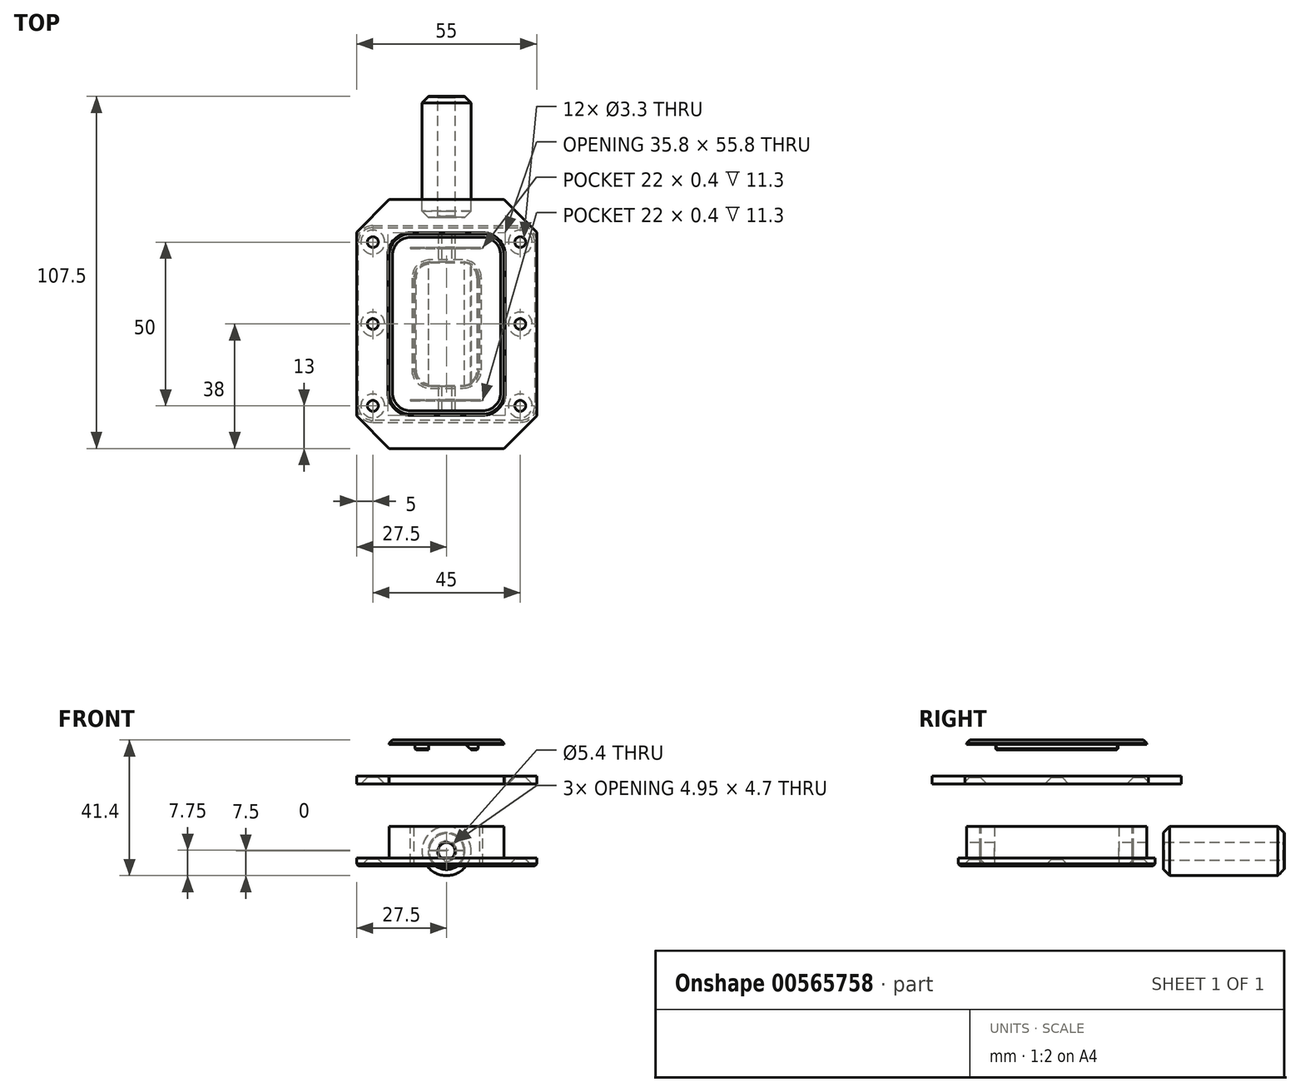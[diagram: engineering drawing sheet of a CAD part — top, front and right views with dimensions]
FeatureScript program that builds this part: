
annotation { "Feature Type Name" : "Feature", "Feature Type Description" : "" }
export const myFeature = defineFeature(function(context is Context, id is Id, definition is map)
    precondition{}
    {
        {
            var Q0;
            Q0=qCreatedBy(makeId("Top.planeOp"),FACE);
            cPlane(context, id + "F0", {"entities" : qUnion([Q0]), "cplaneType" : CPlaneType.OFFSET, "offset" : 25 * mm, "width" : 150 * mm, "height" : 150 * mm});
        }
        {
            var Q0;
            Q0=qCreatedBy(makeId("Top.planeOp"),FACE);
            var sketch = newSketch(context, id + "F1", { "sketchPlane" : qUnion([Q0])});
            skLineSegment(sketch, "E0.bottom", {"start": v(-22.5, 30) * mm, "end": v(22.5, 30) * mm});
            skLineSegment(sketch, "E0.top", {"start": v(-22.5, -30) * mm, "end": v(22.5, -30) * mm});
            skLineSegment(sketch, "E0.left", {"start": v(-27.5, 25) * mm, "end": v(-27.5, -25) * mm});
            skLineSegment(sketch, "E0.right", {"start": v(27.5, 25) * mm, "end": v(27.5, -25) * mm});
            skPoint(sketch, "E1.visualSharp", {"position": v(-27.5, 30) * mm});
            skArc(sketch, "E1.filletArc", {"start": v(-22.5, 30) * mm, "mid": v(-26.04, 28.54) * mm, "end": v(-27.5, 25) * mm});
            skPoint(sketch, "E2.visualSharp", {"position": v(27.5, 30) * mm});
            skArc(sketch, "E2.filletArc", {"start": v(27.5, 25) * mm, "mid": v(26.04, 28.54) * mm, "end": v(22.5, 30) * mm});
            skPoint(sketch, "E3.visualSharp", {"position": v(-27.5, -30) * mm});
            skArc(sketch, "E3.filletArc", {"start": v(-27.5, -25) * mm, "mid": v(-26.04, -28.54) * mm, "end": v(-22.5, -30) * mm});
            skPoint(sketch, "E4.visualSharp", {"position": v(27.5, -30) * mm});
            skArc(sketch, "E4.filletArc", {"start": v(22.5, -30) * mm, "mid": v(26.04, -28.54) * mm, "end": v(27.5, -25) * mm});
            skLineSegment(sketch, "E5.bottom", {"start": v(-5, 19) * mm, "end": v(5, 19) * mm});
            skLineSegment(sketch, "E5.top", {"start": v(-5, -19) * mm, "end": v(5, -19) * mm});
            skLineSegment(sketch, "E5.left", {"start": v(-10, 14) * mm, "end": v(-10, -14) * mm});
            skLineSegment(sketch, "E5.right", {"start": v(10, 14) * mm, "end": v(10, -14) * mm});
            skLineSegment(sketch, "E6", {"start": v(0, 19) * mm, "end": v(0, 30) * mm, "construction": true});
            skLineSegment(sketch, "E7", {"start": v(0, -19) * mm, "end": v(0, -30) * mm, "construction": true});
            skPoint(sketch, "E8.visualSharp", {"position": v(-10, 19) * mm});
            skArc(sketch, "E8.filletArc", {"start": v(-5, 19) * mm, "mid": v(-8.54, 17.54) * mm, "end": v(-10, 14) * mm});
            skPoint(sketch, "E9.visualSharp", {"position": v(10, 19) * mm});
            skArc(sketch, "E9.filletArc", {"start": v(10, 14) * mm, "mid": v(8.54, 17.54) * mm, "end": v(5, 19) * mm});
            skPoint(sketch, "E10.visualSharp", {"position": v(10, -19) * mm});
            skArc(sketch, "E10.filletArc", {"start": v(5, -19) * mm, "mid": v(8.54, -17.54) * mm, "end": v(10, -14) * mm});
            skPoint(sketch, "E11.visualSharp", {"position": v(-10, -19) * mm});
            skArc(sketch, "E11.filletArc", {"start": v(-10, -14) * mm, "mid": v(-8.54, -17.54) * mm, "end": v(-5, -19) * mm});
            skLineSegment(sketch, "E12", {"start": v(-27.5, 30) * mm, "end": v(27.5, -30) * mm, "construction": true});
            skLineSegment(sketch, "E13", {"start": v(27.5, 30) * mm, "end": v(-27.5, -30) * mm, "construction": true});
            skCircle(sketch, "E14", {"center": v(-22.5, 25) * mm, "radius": 1.65 * mm});
            skCircle(sketch, "E15", {"center": v(22.5, 25) * mm, "radius": 1.65 * mm});
            skCircle(sketch, "E16", {"center": v(22.5, -25) * mm, "radius": 1.65 * mm});
            skCircle(sketch, "E17", {"center": v(-22.5, -25) * mm, "radius": 1.65 * mm});
            skLineSegment(sketch, "E18", {"start": v(-22.5, 25) * mm, "end": v(-22.5, -25) * mm, "construction": true});
            skLineSegment(sketch, "E19", {"start": v(22.5, 25) * mm, "end": v(22.5, -25) * mm, "construction": true});
            skCircle(sketch, "E20", {"center": v(-22.5, 0) * mm, "radius": 1.65 * mm});
            skCircle(sketch, "E21", {"center": v(22.5, 0) * mm, "radius": 1.65 * mm});
            skSolve(sketch);
        }
        {
            var Q0;
            Q0=makeQuery(id+"F1.imprint","IMPRINT",FACE,{"disambiguationData":[TD([[makeQuery(id+"F1.imprint","IMPRINT",EDGE,{"derivedFrom":sQuery(id+"F1.wireOp",EDGE,"E0.bottom")}),-1.0]])]});
            extrude(context, id + "F2", {"entities" : qUnion([Q0]), "depth" : 2.4 * mm, "offsetDistance" : 25 * mm});
        }
        {
            var Q0;
            Q0=makeQuery(id+"F2.opExtrude","CAP_FACE",FACE,{"disambiguationData":[OSD([sQuery(id+"F1.wireOp",EDGE,"E0.bottom"),sQuery(id+"F1.wireOp",EDGE,"E0.top"),sQuery(id+"F1.wireOp",EDGE,"E0.left"),sQuery(id+"F1.wireOp",EDGE,"E0.right"),sQuery(id+"F1.wireOp",EDGE,"E1.filletArc"),sQuery(id+"F1.wireOp",EDGE,"E2.filletArc"),sQuery(id+"F1.wireOp",EDGE,"E3.filletArc"),sQuery(id+"F1.wireOp",EDGE,"E4.filletArc")])],"isStart":false});
            var sketch = newSketch(context, id + "F3", { "sketchPlane" : qUnion([Q0])});
            skArc(sketch, "E22.0.0", {"start": v(-27.5, -25) * mm, "mid": v(-26.04, -28.54) * mm, "end": v(-22.5, -30) * mm, "construction": true});
            skLineSegment(sketch, "E22.0.1", {"start": v(-22.5, -30) * mm, "end": v(22.5, -30) * mm, "construction": true});
            skArc(sketch, "E22.0.2", {"start": v(22.5, -30) * mm, "mid": v(26.04, -28.54) * mm, "end": v(27.5, -25) * mm, "construction": true});
            skLineSegment(sketch, "E22.0.3", {"start": v(27.5, -25) * mm, "end": v(27.5, 25) * mm, "construction": true});
            skArc(sketch, "E22.0.4", {"start": v(27.5, 25) * mm, "mid": v(26.04, 28.54) * mm, "end": v(22.5, 30) * mm, "construction": true});
            skLineSegment(sketch, "E22.0.5", {"start": v(22.5, 30) * mm, "end": v(-22.5, 30) * mm, "construction": true});
            skArc(sketch, "E22.0.6", {"start": v(-22.5, 30) * mm, "mid": v(-26.04, 28.54) * mm, "end": v(-27.5, 25) * mm, "construction": true});
            skLineSegment(sketch, "E22.0.7", {"start": v(-27.5, 25) * mm, "end": v(-27.5, -25) * mm, "construction": true});
            skLineSegment(sketch, "E23.bottom", {"start": v(-11, 27.5) * mm, "end": v(11, 27.5) * mm});
            skLineSegment(sketch, "E23.top", {"start": v(-11, -27.5) * mm, "end": v(11, -27.5) * mm});
            skLineSegment(sketch, "E23.left", {"start": v(-17.5, 21) * mm, "end": v(-17.5, -21) * mm});
            skLineSegment(sketch, "E23.right", {"start": v(17.5, 21) * mm, "end": v(17.5, -21) * mm});
            skLineSegment(sketch, "E24", {"start": v(0, 30) * mm, "end": v(0, 27.5) * mm, "construction": true});
            skLineSegment(sketch, "E25", {"start": v(0, -27.5) * mm, "end": v(0, -30) * mm, "construction": true});
            skPoint(sketch, "E26.visualSharp", {"position": v(-17.5, 27.5) * mm});
            skArc(sketch, "E26.filletArc", {"start": v(-11, 27.5) * mm, "mid": v(-15.6, 25.6) * mm, "end": v(-17.5, 21) * mm});
            skPoint(sketch, "E27.visualSharp", {"position": v(17.5, 27.5) * mm});
            skArc(sketch, "E27.filletArc", {"start": v(17.5, 21) * mm, "mid": v(15.6, 25.6) * mm, "end": v(11, 27.5) * mm});
            skPoint(sketch, "E28.visualSharp", {"position": v(-17.5, -27.5) * mm});
            skArc(sketch, "E28.filletArc", {"start": v(-17.5, -21) * mm, "mid": v(-15.6, -25.6) * mm, "end": v(-11, -27.5) * mm});
            skPoint(sketch, "E29.visualSharp", {"position": v(17.5, -27.5) * mm});
            skArc(sketch, "E29.filletArc", {"start": v(11, -27.5) * mm, "mid": v(15.6, -25.6) * mm, "end": v(17.5, -21) * mm});
            skSolve(sketch);
        }
        {
            var Q0;
            Q0=makeQuery(id+"F3.imprint","IMPRINT",FACE,{"disambiguationData":[TD([[makeQuery(id+"F3.imprint","IMPRINT",EDGE,{"derivedFrom":sQuery(id+"F3.wireOp",EDGE,"E23.bottom")}),-1.0]])]});
            extrude(context, id + "F4", {"entities" : qUnion([Q0]), "operationType" : NewBodyOperationType.ADD, "depth" : 9.6 * mm, "offsetDistance" : 25 * mm});
        }
        {
            var Q0;
            Q0=makeQuery(id+"F2.opExtrude","SWEPT_FACE",FACE,{"disambiguationData":[OSD([sQuery(id+"F1.wireOp",EDGE,"E0.top")])]});
            var sketch = newSketch(context, id + "F5", { "sketchPlane" : qUnion([Q0])});
            skLineSegment(sketch, "E30.0.0", {"start": v(-11, 2.4) * mm, "end": v(11, 2.4) * mm, "construction": true});
            skLineSegment(sketch, "E30.0.1", {"start": v(11, 2.4) * mm, "end": v(11, 12) * mm, "construction": true});
            skLineSegment(sketch, "E30.0.2", {"start": v(11, 12) * mm, "end": v(-11, 12) * mm});
            skLineSegment(sketch, "E30.0.3", {"start": v(-11, 12) * mm, "end": v(-11, 2.4) * mm, "construction": true});
            skLineSegment(sketch, "E31", {"start": v(-11, 4.5) * mm, "end": v(11, 4.5) * mm});
            skCircle(sketch, "E32", {"center": v(0, 4.5) * mm, "radius": 2.6 * mm});
            skCircle(sketch, "E33", {"center": v(0, 4.5) * mm, "radius": 7.5 * mm, "construction": true});
            skSolve(sketch);
        }
        {
            var Q0;
            {var subQ0=sQuery(id+"F5.wireOp",EDGE,"E32");var subQ1=sQuery(id+"F5.wireOp",EDGE,"E31");var subQ2=makeQuery(id+"F5.imprint","INTERSECT",VERTEX,{"disambiguationData":[OD(0.0)],"derivedFrom":[subQ1,subQ0]});Q0=makeQuery(id+"F5.imprint","IMPRINT",FACE,{"disambiguationData":[TD([[makeQuery(id+"F5.imprint","IMPRINT",EDGE,{"disambiguationData":[TD([[subQ2,-1.0]])],"derivedFrom":subQ1}),1.0]])]});}
            var Q1;
            {var subQ0=sQuery(id+"F5.wireOp",EDGE,"E32");var subQ1=sQuery(id+"F5.wireOp",EDGE,"E31");var subQ2=makeQuery(id+"F5.imprint","INTERSECT",VERTEX,{"disambiguationData":[OD(0.0)],"derivedFrom":[subQ1,subQ0]});Q1=makeQuery(id+"F5.imprint","IMPRINT",FACE,{"disambiguationData":[TD([[makeQuery(id+"F5.imprint","IMPRINT",EDGE,{"disambiguationData":[TD([[subQ2,-1.0]])],"derivedFrom":subQ1}),-1.0]])]});}
            var Q2;
            {var subQ0=sQuery(id+"F5.wireOp",EDGE,"E32");var subQ1=makeQuery(id+"F2.opExtrude","CAP_EDGE",EDGE,{"disambiguationData":[OSD([sQuery(id+"F1.wireOp",EDGE,"E0.top")])],"isStart":false});var subQ2=makeQuery(id+"F5.imprint","INTERSECT",VERTEX,{"disambiguationData":[OD(0.0)],"derivedFrom":[subQ1,subQ0]});Q2=makeQuery(id+"F5.imprint","IMPRINT",FACE,{"disambiguationData":[TD([[makeQuery(id+"F5.imprint","IMPRINT",EDGE,{"disambiguationData":[TD([[subQ2,-1.0]])],"derivedFrom":subQ0}),1.0]])]});}
            var Q3;
            Q3=makeQuery(id+"F2.opExtrude","SWEPT_FACE",FACE,{"disambiguationData":[OSD([sQuery(id+"F1.wireOp",EDGE,"E0.bottom")])]});
            extrude(context, id + "F6", {"entities" : qUnion([Q0, Q1, Q2]), "operationType" : NewBodyOperationType.REMOVE, "endBound" : BoundingType.UP_TO_SURFACE, "oppositeDirection" : true, "depth" : 25 * mm, "endBoundEntityFace" : qUnion([Q3]), "offsetDistance" : 25 * mm});
        }
        {
            var Q0;
            Q0=qCreatedBy(id+"F0.planeOp",FACE);
            var sketch = newSketch(context, id + "F7", { "sketchPlane" : qUnion([Q0])});
            skArc(sketch, "E34.0", {"start": v(22.5, -30) * mm, "mid": v(26.04, -28.54) * mm, "end": v(27.5, -25) * mm, "construction": true});
            skLineSegment(sketch, "E35.0", {"start": v(27.5, 25) * mm, "end": v(27.5, -25) * mm, "construction": true});
            skLineSegment(sketch, "E36.0", {"start": v(-22.5, -30) * mm, "end": v(22.5, -30) * mm, "construction": true});
            skLineSegment(sketch, "E37.0", {"start": v(-27.5, 25) * mm, "end": v(-27.5, -25) * mm, "construction": true});
            skArc(sketch, "E38.0", {"start": v(-27.5, -25) * mm, "mid": v(-26.04, -28.54) * mm, "end": v(-22.5, -30) * mm, "construction": true});
            skArc(sketch, "E38.1", {"start": v(-22.5, 30) * mm, "mid": v(-26.04, 28.54) * mm, "end": v(-27.5, 25) * mm, "construction": true});
            skLineSegment(sketch, "E38.2", {"start": v(-22.5, 30) * mm, "end": v(22.5, 30) * mm, "construction": true});
            skArc(sketch, "E39.0", {"start": v(27.5, 25) * mm, "mid": v(26.04, 28.54) * mm, "end": v(22.5, 30) * mm, "construction": true});
            skCircle(sketch, "E40.0", {"center": v(22.5, -25) * mm, "radius": 1.65 * mm});
            skCircle(sketch, "E41.0", {"center": v(22.5, 0) * mm, "radius": 1.65 * mm});
            skCircle(sketch, "E42.0", {"center": v(22.5, 25) * mm, "radius": 1.65 * mm});
            skCircle(sketch, "E43.0", {"center": v(-22.5, 25) * mm, "radius": 1.65 * mm});
            skCircle(sketch, "E44.0", {"center": v(-22.5, 0) * mm, "radius": 1.65 * mm});
            skCircle(sketch, "E45.0", {"center": v(-22.5, -25) * mm, "radius": 1.65 * mm});
            skArc(sketch, "E46.0", {"start": v(11, -27.5) * mm, "mid": v(15.6, -25.6) * mm, "end": v(17.5, -21) * mm, "construction": true});
            skLineSegment(sketch, "E47.0", {"start": v(17.5, 21) * mm, "end": v(17.5, -21) * mm, "construction": true});
            skArc(sketch, "E48.0", {"start": v(17.5, 21) * mm, "mid": v(15.6, 25.6) * mm, "end": v(11, 27.5) * mm, "construction": true});
            skLineSegment(sketch, "E49.0", {"start": v(-11, 27.5) * mm, "end": v(11, 27.5) * mm, "construction": true});
            skArc(sketch, "E50.0", {"start": v(-11, 27.5) * mm, "mid": v(-15.6, 25.6) * mm, "end": v(-17.5, 21) * mm, "construction": true});
            skLineSegment(sketch, "E51.0", {"start": v(-17.5, 21) * mm, "end": v(-17.5, -21) * mm, "construction": true});
            skArc(sketch, "E52.0", {"start": v(-17.5, -21) * mm, "mid": v(-15.6, -25.6) * mm, "end": v(-11, -27.5) * mm, "construction": true});
            skLineSegment(sketch, "E53.0", {"start": v(-11, -27.5) * mm, "end": v(11, -27.5) * mm, "construction": true});
            skLineSegment(sketch, "E54.bottom", {"start": v(27.5, -38) * mm, "end": v(-27.5, -38) * mm});
            skLineSegment(sketch, "E54.top", {"start": v(27.5, 38) * mm, "end": v(-27.5, 38) * mm});
            skLineSegment(sketch, "E54.left", {"start": v(27.5, -38) * mm, "end": v(27.5, 38) * mm});
            skLineSegment(sketch, "E54.right", {"start": v(-27.5, -38) * mm, "end": v(-27.5, 38) * mm});
            skArc(sketch, "E55.0", {"start": v(-11, 27.9) * mm, "mid": v(-15.88, 25.88) * mm, "end": v(-17.9, 21) * mm});
            skLineSegment(sketch, "E55.1", {"start": v(-11, 27.9) * mm, "end": v(11, 27.9) * mm});
            skLineSegment(sketch, "E55.2", {"start": v(-17.9, 21) * mm, "end": v(-17.9, -21) * mm});
            skArc(sketch, "E55.3", {"start": v(17.9, 21) * mm, "mid": v(15.88, 25.88) * mm, "end": v(11, 27.9) * mm});
            skArc(sketch, "E55.4", {"start": v(-17.9, -21) * mm, "mid": v(-15.88, -25.88) * mm, "end": v(-11, -27.9) * mm});
            skLineSegment(sketch, "E55.5", {"start": v(-11, -27.9) * mm, "end": v(11, -27.9) * mm});
            skArc(sketch, "E55.6", {"start": v(11, -27.9) * mm, "mid": v(15.88, -25.88) * mm, "end": v(17.9, -21) * mm});
            skLineSegment(sketch, "E55.7", {"start": v(17.9, 21) * mm, "end": v(17.9, -21) * mm});
            skSolve(sketch);
        }
        {
            var Q0;
            Q0=makeQuery(id+"F7.imprint","IMPRINT",FACE,{"disambiguationData":[TD([[makeQuery(id+"F7.imprint","IMPRINT",EDGE,{"derivedFrom":sQuery(id+"F7.wireOp",EDGE,"E40.0")}),-1.0]])]});
            extrude(context, id + "F8", {"entities" : qUnion([Q0]), "depth" : 2.4 * mm, "offsetDistance" : 25 * mm});
        }
        {
            var Q0;
            Q0=makeQuery(id+"F8.opExtrude","SWEPT_EDGE",EDGE,{"disambiguationData":[OSD([sQuery(id+"F7.wireOp",EDGE,"E54.bottom"),sQuery(id+"F7.wireOp",EDGE,"E54.left")])]});
            var Q1;
            Q1=makeQuery(id+"F8.opExtrude","SWEPT_EDGE",EDGE,{"disambiguationData":[OSD([sQuery(id+"F7.wireOp",EDGE,"E54.top"),sQuery(id+"F7.wireOp",EDGE,"E54.left")])]});
            var Q2;
            Q2=makeQuery(id+"F8.opExtrude","SWEPT_EDGE",EDGE,{"disambiguationData":[OSD([sQuery(id+"F7.wireOp",EDGE,"E54.top"),sQuery(id+"F7.wireOp",EDGE,"E54.right")])]});
            var Q3;
            Q3=makeQuery(id+"F8.opExtrude","SWEPT_EDGE",EDGE,{"disambiguationData":[OSD([sQuery(id+"F7.wireOp",EDGE,"E54.bottom"),sQuery(id+"F7.wireOp",EDGE,"E54.right")])]});
            chamfer(context, id + "F9", {"entities" : qUnion([Q0, Q1, Q2, Q3]), "width" : 10 * mm, "tangentPropagation" : true});
        }
        {
            var Q0;
            Q0=makeQuery(id+"F2.opExtrude","CAP_EDGE",EDGE,{"disambiguationData":[OSD([sQuery(id+"F1.wireOp",EDGE,"E17")])],"isStart":true});
            var Q1;
            Q1=makeQuery(id+"F2.opExtrude","CAP_EDGE",EDGE,{"disambiguationData":[OSD([sQuery(id+"F1.wireOp",EDGE,"E14")])],"isStart":true});
            var Q2;
            Q2=makeQuery(id+"F2.opExtrude","CAP_EDGE",EDGE,{"disambiguationData":[OSD([sQuery(id+"F1.wireOp",EDGE,"E15")])],"isStart":true});
            var Q3;
            Q3=makeQuery(id+"F2.opExtrude","CAP_EDGE",EDGE,{"disambiguationData":[OSD([sQuery(id+"F1.wireOp",EDGE,"E16")])],"isStart":true});
            var Q4;
            Q4=makeQuery(id+"F2.opExtrude","CAP_EDGE",EDGE,{"disambiguationData":[OSD([sQuery(id+"F1.wireOp",EDGE,"E21")])],"isStart":true});
            var Q5;
            Q5=makeQuery(id+"F2.opExtrude","CAP_EDGE",EDGE,{"disambiguationData":[OSD([sQuery(id+"F1.wireOp",EDGE,"E20")])],"isStart":true});
            var Q6;
            Q6=makeQuery(id+"F8.opExtrude","CAP_EDGE",EDGE,{"disambiguationData":[OSD([sQuery(id+"F7.wireOp",EDGE,"E40.0")])],"isStart":true});
            var Q7;
            Q7=makeQuery(id+"F8.opExtrude","CAP_EDGE",EDGE,{"disambiguationData":[OSD([sQuery(id+"F7.wireOp",EDGE,"E41.0")])],"isStart":true});
            var Q8;
            Q8=makeQuery(id+"F8.opExtrude","CAP_EDGE",EDGE,{"disambiguationData":[OSD([sQuery(id+"F7.wireOp",EDGE,"E42.0")])],"isStart":true});
            var Q9;
            Q9=makeQuery(id+"F8.opExtrude","CAP_EDGE",EDGE,{"disambiguationData":[OSD([sQuery(id+"F7.wireOp",EDGE,"E43.0")])],"isStart":true});
            var Q10;
            Q10=makeQuery(id+"F8.opExtrude","CAP_EDGE",EDGE,{"disambiguationData":[OSD([sQuery(id+"F7.wireOp",EDGE,"E44.0")])],"isStart":true});
            var Q11;
            Q11=makeQuery(id+"F8.opExtrude","CAP_EDGE",EDGE,{"disambiguationData":[OSD([sQuery(id+"F7.wireOp",EDGE,"E45.0")])],"isStart":true});
            chamfer(context, id + "F10", {"entities" : qUnion([Q0, Q1, Q2, Q3, Q4, Q5, Q6, Q7, Q8, Q9, Q10, Q11]), "width" : 2 * mm, "tangentPropagation" : true});
        }
        {
            var Q0;
            {var subQ0=sQuery(id+"F1.wireOp",EDGE,"E5.bottom");Q0=makeQuery(id+"F4.boolean.opBoolean","MERGE",FACE,{"derivedFrom":[makeQuery(id+"F2.opExtrude","SWEPT_FACE",FACE,{"disambiguationData":[OSD([subQ0])]}),makeQuery(id+"F4.opExtrude","SWEPT_FACE",FACE,{"disambiguationData":[OSD([subQ0])]})]});}
            cPlane(context, id + "F11", {"entities" : qUnion([Q0]), "cplaneType" : CPlaneType.OFFSET, "offset" : 50.5 * mm, "oppositeDirection" : true, "width" : 150 * mm, "height" : 150 * mm});
        }
        {
            var Q0;
            Q0=qCreatedBy(id+"F11.planeOp",FACE);
            var sketch = newSketch(context, id + "F12", { "sketchPlane" : qUnion([Q0])});
            skCircle(sketch, "E56.0", {"center": v(0, 4.5) * mm, "radius": 2.6 * mm, "construction": true});
            skCircle(sketch, "E57", {"center": v(0, 4.5) * mm, "radius": 7.5 * mm});
            skCircle(sketch, "E58", {"center": v(0, 4.5) * mm, "radius": 2.7 * mm});
            skSolve(sketch);
        }
        {
            var Q0;
            Q0=makeQuery(id+"F12.imprint","IMPRINT",FACE,{"disambiguationData":[TD([[makeQuery(id+"F12.imprint","IMPRINT",EDGE,{"derivedFrom":sQuery(id+"F12.wireOp",EDGE,"E57")}),1.0]])]});
            extrude(context, id + "F13", {"entities" : qUnion([Q0]), "depth" : 37 * mm, "offsetDistance" : 25 * mm});
        }
        {
            var Q0;
            Q0=makeQuery(id+"F13.opExtrude","CAP_EDGE",EDGE,{"disambiguationData":[OSD([sQuery(id+"F12.wireOp",EDGE,"E57")])],"isStart":true});
            var Q1;
            Q1=makeQuery(id+"F13.opExtrude","CAP_EDGE",EDGE,{"disambiguationData":[OSD([sQuery(id+"F12.wireOp",EDGE,"E57")])],"isStart":false});
            chamfer(context, id + "F14", {"entities" : qUnion([Q0, Q1]), "width" : 2 * mm, "tangentPropagation" : true});
        }
        {
            var Q0;
            Q0=makeQuery(id+"F13.opExtrude","CAP_FACE",FACE,{"disambiguationData":[OSD([sQuery(id+"F12.wireOp",EDGE,"E56.0"),sQuery(id+"F12.wireOp",EDGE,"E57")])],"isStart":true});
            var Q1;
            Q1=makeQuery(id+"F13.opExtrude","CAP_FACE",FACE,{"disambiguationData":[OSD([sQuery(id+"F12.wireOp",EDGE,"E56.0"),sQuery(id+"F12.wireOp",EDGE,"E57")])],"isStart":false});
            chamfer(context, id + "F15", {"entities" : qUnion([Q0, Q1]), "width" : .4 * mm, "tangentPropagation" : true});
        }
        {
            var Q0;
            Q0=makeQuery(id+"F2.opExtrude","CAP_EDGE",EDGE,{"disambiguationData":[OSD([sQuery(id+"F1.wireOp",EDGE,"E0.top")])],"isStart":true});
            var Q1;
            Q1=makeQuery(id+"F2.opExtrude","CAP_EDGE",EDGE,{"disambiguationData":[OSD([sQuery(id+"F1.wireOp",EDGE,"E5.left")])],"isStart":true});
            chamfer(context, id + "F16", {"entities" : qUnion([Q0, Q1]), "width" : .6 * mm, "tangentPropagation" : true});
        }
        {
            var Q0;
            Q0=makeQuery(id+"F4.opExtrude","CAP_FACE",FACE,{"disambiguationData":[OSD([sQuery(id+"F1.wireOp",EDGE,"E5.bottom"),sQuery(id+"F1.wireOp",EDGE,"E5.top"),sQuery(id+"F1.wireOp",EDGE,"E5.left"),sQuery(id+"F1.wireOp",EDGE,"E5.right"),sQuery(id+"F1.wireOp",EDGE,"E8.filletArc"),sQuery(id+"F1.wireOp",EDGE,"E9.filletArc"),sQuery(id+"F1.wireOp",EDGE,"E10.filletArc"),sQuery(id+"F1.wireOp",EDGE,"E11.filletArc"),sQuery(id+"F3.wireOp",EDGE,"E23.bottom"),sQuery(id+"F3.wireOp",EDGE,"E23.top"),sQuery(id+"F3.wireOp",EDGE,"E23.left"),sQuery(id+"F3.wireOp",EDGE,"E23.right"),sQuery(id+"F3.wireOp",EDGE,"E26.filletArc"),sQuery(id+"F3.wireOp",EDGE,"E27.filletArc"),sQuery(id+"F3.wireOp",EDGE,"E28.filletArc"),sQuery(id+"F3.wireOp",EDGE,"E29.filletArc")])],"isStart":false});
            cPlane(context, id + "F17", {"entities" : qUnion([Q0]), "cplaneType" : CPlaneType.OFFSET, "offset" : 25 * mm, "width" : 150 * mm, "height" : 150 * mm});
        }
        {
            var Q0;
            Q0=qCreatedBy(id+"F17.planeOp",FACE);
            var sketch = newSketch(context, id + "F18", { "sketchPlane" : qUnion([Q0])});
            skArc(sketch, "E59.0.0", {"start": v(-17.5, -21) * mm, "mid": v(-15.6, -25.6) * mm, "end": v(-11, -27.5) * mm});
            skLineSegment(sketch, "E59.0.1", {"start": v(-11, -27.5) * mm, "end": v(11, -27.5) * mm});
            skArc(sketch, "E59.0.2", {"start": v(11, -27.5) * mm, "mid": v(15.6, -25.6) * mm, "end": v(17.5, -21) * mm});
            skLineSegment(sketch, "E59.0.3", {"start": v(17.5, -21) * mm, "end": v(17.5, 21) * mm});
            skArc(sketch, "E59.0.4", {"start": v(17.5, 21) * mm, "mid": v(15.6, 25.6) * mm, "end": v(11, 27.5) * mm});
            skLineSegment(sketch, "E59.0.5", {"start": v(11, 27.5) * mm, "end": v(-11, 27.5) * mm});
            skArc(sketch, "E59.0.6", {"start": v(-11, 27.5) * mm, "mid": v(-15.6, 25.6) * mm, "end": v(-17.5, 21) * mm});
            skLineSegment(sketch, "E59.0.7", {"start": v(-17.5, 21) * mm, "end": v(-17.5, -21) * mm});
            skSolve(sketch);
        }
        {
            var Q0;
            Q0 = qSketchRegion(id + "F18", true);
            extrude(context, id + "F19", {"entities" : qUnion([Q0]), "depth" : 1.4 * mm, "offsetDistance" : 25 * mm});
        }
        {
            var Q0;
            Q0=makeQuery(id+"F19.opExtrude","CAP_FACE",FACE,{"disambiguationData":[OSD([sQuery(id+"F18.wireOp",EDGE,"E59.0.0"),sQuery(id+"F18.wireOp",EDGE,"E59.0.1"),sQuery(id+"F18.wireOp",EDGE,"E59.0.2"),sQuery(id+"F18.wireOp",EDGE,"E59.0.3"),sQuery(id+"F18.wireOp",EDGE,"E59.0.4"),sQuery(id+"F18.wireOp",EDGE,"E59.0.5"),sQuery(id+"F18.wireOp",EDGE,"E59.0.6"),sQuery(id+"F18.wireOp",EDGE,"E59.0.7")])],"isStart":true});
            var sketch = newSketch(context, id + "F20", { "sketchPlane" : qUnion([Q0])});
            skLineSegment(sketch, "E60.0", {"start": v(-10, -14) * mm, "end": v(-10, 14) * mm, "construction": true});
            skArc(sketch, "E61.0", {"start": v(-5, -19) * mm, "mid": v(-8.54, -17.54) * mm, "end": v(-10, -14) * mm, "construction": true});
            skLineSegment(sketch, "E62.0", {"start": v(-5, -19) * mm, "end": v(5, -19) * mm, "construction": true});
            skArc(sketch, "E63.0", {"start": v(10, -14) * mm, "mid": v(8.54, -17.54) * mm, "end": v(5, -19) * mm, "construction": true});
            skLineSegment(sketch, "E64.0", {"start": v(10, -14) * mm, "end": v(10, 14) * mm, "construction": true});
            skArc(sketch, "E65.0", {"start": v(5, 19) * mm, "mid": v(8.54, 17.54) * mm, "end": v(10, 14) * mm, "construction": true});
            skLineSegment(sketch, "E66.0", {"start": v(-5, 19) * mm, "end": v(5, 19) * mm, "construction": true});
            skArc(sketch, "E67.0", {"start": v(-10, 14) * mm, "mid": v(-8.54, 17.54) * mm, "end": v(-5, 19) * mm, "construction": true});
            skLineSegment(sketch, "E68.0", {"start": v(-5, -18.7) * mm, "end": v(5, -18.7) * mm});
            skArc(sketch, "E68.1", {"start": v(9.7, -14) * mm, "mid": v(8.32, -17.32) * mm, "end": v(5, -18.7) * mm});
            skArc(sketch, "E68.2", {"start": v(-5, -18.7) * mm, "mid": v(-8.32, -17.32) * mm, "end": v(-9.7, -14) * mm});
            skLineSegment(sketch, "E68.3", {"start": v(9.7, -14) * mm, "end": v(9.7, 14) * mm});
            skLineSegment(sketch, "E68.4", {"start": v(-9.7, -14) * mm, "end": v(-9.7, 14) * mm});
            skArc(sketch, "E68.5", {"start": v(-9.7, 14) * mm, "mid": v(-8.32, 17.32) * mm, "end": v(-5, 18.7) * mm});
            skLineSegment(sketch, "E68.6", {"start": v(-5, 18.7) * mm, "end": v(5, 18.7) * mm});
            skArc(sketch, "E68.7", {"start": v(5, 18.7) * mm, "mid": v(8.32, 17.32) * mm, "end": v(9.7, 14) * mm});
            skSolve(sketch);
        }
        {
            var Q0;
            Q0 = qSketchRegion(id + "F20", true);
            extrude(context, id + "F21", {"entities" : qUnion([Q0]), "operationType" : NewBodyOperationType.ADD, "depth" : 1.6 * mm, "offsetDistance" : 25 * mm});
        }
        {
            var Q0;
            Q0=makeQuery(id+"F21.opExtrude","CAP_FACE",FACE,{"disambiguationData":[OSD([sQuery(id+"F20.wireOp",EDGE,"E68.0"),sQuery(id+"F20.wireOp",EDGE,"E68.1"),sQuery(id+"F20.wireOp",EDGE,"E68.2"),sQuery(id+"F20.wireOp",EDGE,"E68.3"),sQuery(id+"F20.wireOp",EDGE,"E68.4"),sQuery(id+"F20.wireOp",EDGE,"E68.5"),sQuery(id+"F20.wireOp",EDGE,"E68.6"),sQuery(id+"F20.wireOp",EDGE,"E68.7")])],"isStart":false});
            var sketch = newSketch(context, id + "F22", { "sketchPlane" : qUnion([Q0])});
            skArc(sketch, "E69.0.0", {"start": v(9.7, 14) * mm, "mid": v(8.32, 17.32) * mm, "end": v(5, 18.7) * mm, "construction": true});
            skLineSegment(sketch, "E69.0.1", {"start": v(5, 18.7) * mm, "end": v(-5, 18.7) * mm, "construction": true});
            skArc(sketch, "E69.0.2", {"start": v(-5, 18.7) * mm, "mid": v(-8.32, 17.32) * mm, "end": v(-9.7, 14) * mm, "construction": true});
            skLineSegment(sketch, "E69.0.3", {"start": v(-9.7, 14) * mm, "end": v(-9.7, -14) * mm, "construction": true});
            skArc(sketch, "E69.0.4", {"start": v(-9.7, -14) * mm, "mid": v(-8.32, -17.32) * mm, "end": v(-5, -18.7) * mm, "construction": true});
            skLineSegment(sketch, "E69.0.5", {"start": v(-5, -18.7) * mm, "end": v(5, -18.7) * mm, "construction": true});
            skArc(sketch, "E69.0.6", {"start": v(5, -18.7) * mm, "mid": v(8.32, -17.32) * mm, "end": v(9.7, -14) * mm, "construction": true});
            skLineSegment(sketch, "E69.0.7", {"start": v(9.7, -14) * mm, "end": v(9.7, 14) * mm, "construction": true});
            skLineSegment(sketch, "E70.bottom", {"start": v(-5.5, 21) * mm, "end": v(5.5, 21) * mm});
            skLineSegment(sketch, "E70.top", {"start": v(-5.5, -21) * mm, "end": v(5.5, -21) * mm});
            skLineSegment(sketch, "E70.left", {"start": v(-5.5, 21) * mm, "end": v(-5.5, -21) * mm});
            skLineSegment(sketch, "E70.right", {"start": v(5.5, 21) * mm, "end": v(5.5, -21) * mm});
            skLineSegment(sketch, "E71", {"start": v(0, 21) * mm, "end": v(0, 18.7) * mm, "construction": true});
            skLineSegment(sketch, "E72", {"start": v(0, -21) * mm, "end": v(0, -18.7) * mm, "construction": true});
            skLineSegment(sketch, "E73", {"start": v(0, -18.7) * mm, "end": v(0, 18.7) * mm, "construction": true});
            skLineSegment(sketch, "E74", {"start": v(0, 0) * mm, "end": v(5.5, 0) * mm, "construction": true});
            skLineSegment(sketch, "E75", {"start": v(0, 0) * mm, "end": v(-5.5, 0) * mm, "construction": true});
            skSolve(sketch);
        }
        {
            var Q0;
            {var subQ9=makeQuery(id+"F21.opExtrude","CAP_EDGE",EDGE,{"disambiguationData":[OSD([sQuery(id+"F20.wireOp",EDGE,"E68.0")])],"isStart":false});Q0=makeQuery(id+"F22.imprint","IMPRINT",FACE,{"disambiguationData":[TD([[makeQuery(id+"F22.imprint","IMPRINT",EDGE,{"derivedFrom":subQ9}),1.0]])]});}
            extrude(context, id + "F23", {"entities" : qUnion([Q0]), "operationType" : NewBodyOperationType.REMOVE, "oppositeDirection" : true, "depth" : 2 * mm, "offsetDistance" : 25 * mm});
        }
        {
            var Q0;
            Q0=makeQuery(id+"F23.boolean.opBoolean","COPY",EDGE,{"derivedFrom":makeQuery(id+"F23.opExtrude","CAP_EDGE",EDGE,{"disambiguationData":[OSD([sQuery(id+"F22.wireOp",EDGE,"E70.right")])],"isStart":true})});
            var Q1;
            Q1=makeQuery(id+"F23.boolean.opBoolean","COPY",EDGE,{"derivedFrom":makeQuery(id+"F23.opExtrude","CAP_EDGE",EDGE,{"disambiguationData":[OSD([sQuery(id+"F22.wireOp",EDGE,"E70.left")])],"isStart":true})});
            chamfer(context, id + "F24", {"entities" : qUnion([Q0, Q1]), "width" : 2 * mm, "tangentPropagation" : true});
        }
        {
            var Q0;
            Q0=makeQuery(id+"F21.opExtrude","CAP_EDGE",EDGE,{"disambiguationData":[OSD([sQuery(id+"F20.wireOp",EDGE,"E68.6")])],"isStart":true});
            var Q1;
            Q1=makeQuery(id+"F21.opExtrude","CAP_EDGE",EDGE,{"disambiguationData":[OSD([sQuery(id+"F20.wireOp",EDGE,"E68.0")])],"isStart":true});
            var Q2;
            Q2=makeQuery(id+"F21.opExtrude","CAP_EDGE",EDGE,{"disambiguationData":[OSD([sQuery(id+"F20.wireOp",EDGE,"E68.3")])],"isStart":false});
            var Q3;
            Q3=makeQuery(id+"F21.opExtrude","CAP_EDGE",EDGE,{"disambiguationData":[OSD([sQuery(id+"F20.wireOp",EDGE,"E68.4")])],"isStart":false});
            var Q4;
            {var subQ0=sQuery(id+"F20.wireOp",EDGE,"E68.1");var subQ1=sQuery(id+"F20.wireOp",EDGE,"E68.3");var subQ2=sQuery(id+"F20.wireOp",EDGE,"E68.7");var subQ3=sQuery(id+"F22.wireOp",EDGE,"E70.right");Q4=makeQuery(id+"F24.opChamfer","BLEND_EDGE",EDGE,{"blendedFrom":[makeQuery(id+"F23.boolean.opBoolean","COPY",EDGE,{"derivedFrom":makeQuery(id+"F23.opExtrude","CAP_EDGE",EDGE,{"disambiguationData":[OSD([subQ3])],"isStart":true})}),makeQuery(id+"F23.boolean.opBoolean","SPLIT",FACE,{"disambiguationData":[TD([makeQuery(id+"F21.opExtrude","SWEPT_FACE",FACE,{"disambiguationData":[OSD([subQ0])]})])],"derivedFrom":makeQuery(id+"F21.opExtrude","CAP_FACE",FACE,{"disambiguationData":[OSD([sQuery(id+"F20.wireOp",EDGE,"E68.0"),subQ0,sQuery(id+"F20.wireOp",EDGE,"E68.2"),subQ1,sQuery(id+"F20.wireOp",EDGE,"E68.4"),sQuery(id+"F20.wireOp",EDGE,"E68.5"),sQuery(id+"F20.wireOp",EDGE,"E68.6"),subQ2])],"isStart":false})})],"blendedInto":[makeQuery(id+"F23.boolean.opBoolean","SPLIT",FACE,{"disambiguationData":[TD([makeQuery(id+"F21.opExtrude","SWEPT_FACE",FACE,{"disambiguationData":[OSD([subQ0])]})])],"derivedFrom":makeQuery(id+"F21.opExtrude","CAP_FACE",FACE,{"disambiguationData":[OSD([sQuery(id+"F20.wireOp",EDGE,"E68.0"),subQ0,sQuery(id+"F20.wireOp",EDGE,"E68.2"),subQ1,sQuery(id+"F20.wireOp",EDGE,"E68.4"),sQuery(id+"F20.wireOp",EDGE,"E68.5"),sQuery(id+"F20.wireOp",EDGE,"E68.6"),subQ2])],"isStart":false})})]});}
            var Q5;
            {var subQ0=sQuery(id+"F20.wireOp",EDGE,"E68.2");var subQ1=sQuery(id+"F22.wireOp",EDGE,"E70.left");var subQ2=sQuery(id+"F20.wireOp",EDGE,"E68.4");var subQ3=sQuery(id+"F20.wireOp",EDGE,"E68.5");Q5=makeQuery(id+"F24.opChamfer","BLEND_EDGE",EDGE,{"blendedFrom":[makeQuery(id+"F23.boolean.opBoolean","COPY",EDGE,{"derivedFrom":makeQuery(id+"F23.opExtrude","CAP_EDGE",EDGE,{"disambiguationData":[OSD([subQ1])],"isStart":true})}),makeQuery(id+"F23.boolean.opBoolean","SPLIT",FACE,{"disambiguationData":[TD([makeQuery(id+"F21.opExtrude","SWEPT_FACE",FACE,{"disambiguationData":[OSD([subQ0])]})])],"derivedFrom":makeQuery(id+"F21.opExtrude","CAP_FACE",FACE,{"disambiguationData":[OSD([sQuery(id+"F20.wireOp",EDGE,"E68.0"),sQuery(id+"F20.wireOp",EDGE,"E68.1"),subQ0,sQuery(id+"F20.wireOp",EDGE,"E68.3"),subQ2,subQ3,sQuery(id+"F20.wireOp",EDGE,"E68.6"),sQuery(id+"F20.wireOp",EDGE,"E68.7")])],"isStart":false})})],"blendedInto":[makeQuery(id+"F23.boolean.opBoolean","SPLIT",FACE,{"disambiguationData":[TD([makeQuery(id+"F21.opExtrude","SWEPT_FACE",FACE,{"disambiguationData":[OSD([subQ0])]})])],"derivedFrom":makeQuery(id+"F21.opExtrude","CAP_FACE",FACE,{"disambiguationData":[OSD([sQuery(id+"F20.wireOp",EDGE,"E68.0"),sQuery(id+"F20.wireOp",EDGE,"E68.1"),subQ0,sQuery(id+"F20.wireOp",EDGE,"E68.3"),subQ2,subQ3,sQuery(id+"F20.wireOp",EDGE,"E68.6"),sQuery(id+"F20.wireOp",EDGE,"E68.7")])],"isStart":false})})]});}
            chamfer(context, id + "F25", {"entities" : qUnion([Q0, Q1, Q2, Q3, Q4, Q5]), "width" : .4 * mm, "tangentPropagation" : true});
        }
        {
            var Q0;
            Q0=makeQuery(id+"F19.opExtrude","CAP_FACE",FACE,{"disambiguationData":[OSD([sQuery(id+"F18.wireOp",EDGE,"E59.0.0"),sQuery(id+"F18.wireOp",EDGE,"E59.0.1"),sQuery(id+"F18.wireOp",EDGE,"E59.0.2"),sQuery(id+"F18.wireOp",EDGE,"E59.0.3"),sQuery(id+"F18.wireOp",EDGE,"E59.0.4"),sQuery(id+"F18.wireOp",EDGE,"E59.0.5"),sQuery(id+"F18.wireOp",EDGE,"E59.0.6"),sQuery(id+"F18.wireOp",EDGE,"E59.0.7")])],"isStart":false});
            chamfer(context, id + "F26", {"entities" : qUnion([Q0]), "width" : 1 * mm, "tangentPropagation" : true});
        }
        {
            var Q0;
            Q0=makeQuery(id+"F4.opExtrude","CAP_FACE",FACE,{"disambiguationData":[OSD([sQuery(id+"F1.wireOp",EDGE,"E5.bottom"),sQuery(id+"F1.wireOp",EDGE,"E5.top"),sQuery(id+"F1.wireOp",EDGE,"E5.left"),sQuery(id+"F1.wireOp",EDGE,"E5.right"),sQuery(id+"F1.wireOp",EDGE,"E8.filletArc"),sQuery(id+"F1.wireOp",EDGE,"E9.filletArc"),sQuery(id+"F1.wireOp",EDGE,"E10.filletArc"),sQuery(id+"F1.wireOp",EDGE,"E11.filletArc"),sQuery(id+"F3.wireOp",EDGE,"E23.bottom"),sQuery(id+"F3.wireOp",EDGE,"E23.top"),sQuery(id+"F3.wireOp",EDGE,"E23.left"),sQuery(id+"F3.wireOp",EDGE,"E23.right"),sQuery(id+"F3.wireOp",EDGE,"E26.filletArc"),sQuery(id+"F3.wireOp",EDGE,"E27.filletArc"),sQuery(id+"F3.wireOp",EDGE,"E28.filletArc"),sQuery(id+"F3.wireOp",EDGE,"E29.filletArc")])],"isStart":false});
            var sketch = newSketch(context, id + "F27", { "sketchPlane" : qUnion([Q0])});
            skArc(sketch, "E76.0.0", {"start": v(-17.5, -21) * mm, "mid": v(-15.6, -25.6) * mm, "end": v(-11, -27.5) * mm, "construction": true});
            skLineSegment(sketch, "E76.0.1", {"start": v(-11, -27.5) * mm, "end": v(11, -27.5) * mm, "construction": true});
            skArc(sketch, "E76.0.2", {"start": v(11, -27.5) * mm, "mid": v(15.6, -25.6) * mm, "end": v(17.5, -21) * mm, "construction": true});
            skLineSegment(sketch, "E76.0.3", {"start": v(17.5, -21) * mm, "end": v(17.5, 21) * mm, "construction": true});
            skArc(sketch, "E76.0.4", {"start": v(17.5, 21) * mm, "mid": v(15.6, 25.6) * mm, "end": v(11, 27.5) * mm, "construction": true});
            skLineSegment(sketch, "E76.0.5", {"start": v(11, 27.5) * mm, "end": v(-11, 27.5) * mm, "construction": true});
            skArc(sketch, "E76.0.6", {"start": v(-11, 27.5) * mm, "mid": v(-15.6, 25.6) * mm, "end": v(-17.5, 21) * mm, "construction": true});
            skLineSegment(sketch, "E76.0.7", {"start": v(-17.5, 21) * mm, "end": v(-17.5, -21) * mm, "construction": true});
            skLineSegment(sketch, "E77.bottom", {"start": v(-11, 23.45) * mm, "end": v(11, 23.45) * mm});
            skLineSegment(sketch, "E77.top", {"start": v(-11, 23.05) * mm, "end": v(11, 23.05) * mm});
            skLineSegment(sketch, "E77.left", {"start": v(-11, 23.45) * mm, "end": v(-11, 23.05) * mm});
            skLineSegment(sketch, "E77.right", {"start": v(11, 23.45) * mm, "end": v(11, 23.05) * mm});
            skLineSegment(sketch, "E78", {"start": v(-11, 27.5) * mm, "end": v(-11, -27.5) * mm, "construction": true});
            skLineSegment(sketch, "E79", {"start": v(11, -27.5) * mm, "end": v(11, 27.5) * mm, "construction": true});
            skLineSegment(sketch, "E80", {"start": v(0, 27.5) * mm, "end": v(0, 23.45) * mm, "construction": true});
            skLineSegment(sketch, "E81", {"start": v(0, 19) * mm, "end": v(0, 23.05) * mm, "construction": true});
            skLineSegment(sketch, "E82", {"start": v(0, -19) * mm, "end": v(0, -23.05) * mm, "construction": true});
            skLineSegment(sketch, "E83", {"start": v(0, -27.5) * mm, "end": v(0, -23.45) * mm, "construction": true});
            skLineSegment(sketch, "E84.bottom", {"start": v(-11, -23.05) * mm, "end": v(11, -23.05) * mm});
            skLineSegment(sketch, "E84.top", {"start": v(-11, -23.45) * mm, "end": v(11, -23.45) * mm});
            skLineSegment(sketch, "E84.left", {"start": v(-11, -23.05) * mm, "end": v(-11, -23.45) * mm});
            skLineSegment(sketch, "E84.right", {"start": v(11, -23.05) * mm, "end": v(11, -23.45) * mm});
            skSolve(sketch);
        }
        {
            var Q0;
            Q0=makeQuery(id+"F27.imprint","IMPRINT",FACE,{"disambiguationData":[TD([[makeQuery(id+"F27.imprint","IMPRINT",EDGE,{"derivedFrom":sQuery(id+"F27.wireOp",EDGE,"E77.bottom")}),-1.0]])]});
            var Q1;
            Q1=makeQuery(id+"F27.imprint","IMPRINT",FACE,{"disambiguationData":[TD([[makeQuery(id+"F27.imprint","IMPRINT",EDGE,{"derivedFrom":sQuery(id+"F27.wireOp",EDGE,"E84.bottom")}),-1.0]])]});
            var Q2;
            {var subQ0=sQuery(id+"F1.wireOp",EDGE,"E2.filletArc");var subQ1=sQuery(id+"F1.wireOp",EDGE,"E21");var subQ2=sQuery(id+"F1.wireOp",EDGE,"E0.bottom");var subQ3=sQuery(id+"F1.wireOp",EDGE,"E15");var subQ4=sQuery(id+"F1.wireOp",EDGE,"E16");var subQ5=sQuery(id+"F1.wireOp",EDGE,"E4.filletArc");var subQ6=sQuery(id+"F1.wireOp",EDGE,"E0.right");var subQ7=sQuery(id+"F1.wireOp",EDGE,"E0.top");Q2=makeQuery(id+"F6.boolean.opBoolean","SPLIT",FACE,{"disambiguationData":[TD([makeQuery(id+"F2.opExtrude","SWEPT_FACE",FACE,{"disambiguationData":[OSD([subQ6])]})])],"derivedFrom":makeQuery(id+"F2.opExtrude","CAP_FACE",FACE,{"disambiguationData":[OSD([subQ2,subQ7,sQuery(id+"F1.wireOp",EDGE,"E0.left"),subQ6,sQuery(id+"F1.wireOp",EDGE,"E1.filletArc"),subQ0,sQuery(id+"F1.wireOp",EDGE,"E3.filletArc"),subQ5,sQuery(id+"F1.wireOp",EDGE,"E5.bottom"),sQuery(id+"F1.wireOp",EDGE,"E5.top"),sQuery(id+"F1.wireOp",EDGE,"E5.left"),sQuery(id+"F1.wireOp",EDGE,"E5.right"),sQuery(id+"F1.wireOp",EDGE,"E8.filletArc"),sQuery(id+"F1.wireOp",EDGE,"E9.filletArc"),sQuery(id+"F1.wireOp",EDGE,"E10.filletArc"),sQuery(id+"F1.wireOp",EDGE,"E11.filletArc"),sQuery(id+"F1.wireOp",EDGE,"E14"),subQ3,subQ4,sQuery(id+"F1.wireOp",EDGE,"E17"),sQuery(id+"F1.wireOp",EDGE,"E20"),subQ1])],"isStart":false})});}
            extrude(context, id + "F28", {"entities" : qUnion([Q0, Q1]), "operationType" : NewBodyOperationType.REMOVE, "oppositeDirection" : true, "depth" : 11.3 * mm, "endBoundEntityFace" : qUnion([Q2]), "offsetDistance" : 25 * mm});
        }
    });
